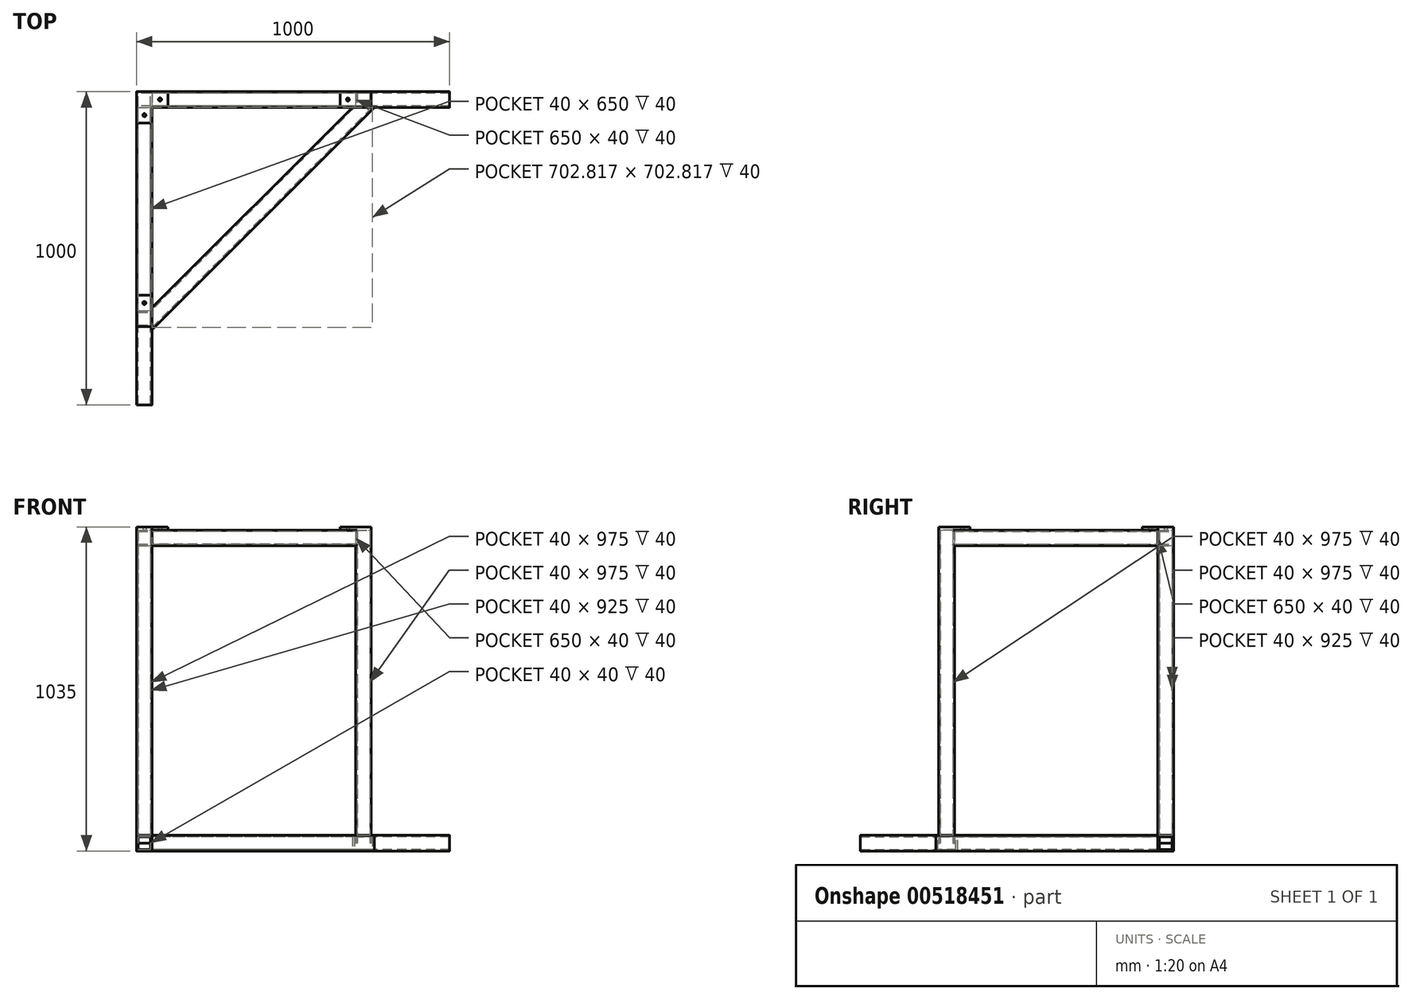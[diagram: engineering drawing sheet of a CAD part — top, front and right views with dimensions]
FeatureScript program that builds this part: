
annotation { "Feature Type Name" : "Feature", "Feature Type Description" : "" }
export const myFeature = defineFeature(function(context is Context, id is Id, definition is map)
    precondition{}
    {
        {
            var Q0;
            Q0=qCreatedBy(makeId("Right.planeOp"),FACE);
            var sketch = newSketch(context, id + "F0", { "sketchPlane" : qUnion([Q0])});
            skLineSegment(sketch, "E0.bottom", {"start": v(20, -25) * mm, "end": v(-20, -25) * mm});
            skLineSegment(sketch, "E0.top", {"start": v(20, 25) * mm, "end": v(-20, 25) * mm});
            skLineSegment(sketch, "E0.left", {"start": v(25, -20) * mm, "end": v(25, 20) * mm});
            skLineSegment(sketch, "E0.right", {"start": v(-25, -20) * mm, "end": v(-25, 20) * mm});
            skPoint(sketch, "E0.middle", {"position": v(0, 0) * mm});
            skLineSegment(sketch, "E1.bottom", {"start": v(20, -20) * mm, "end": v(-20, -20) * mm});
            skLineSegment(sketch, "E1.top", {"start": v(20, 20) * mm, "end": v(-20, 20) * mm});
            skLineSegment(sketch, "E1.left", {"start": v(20, -20) * mm, "end": v(20, 20) * mm});
            skLineSegment(sketch, "E1.right", {"start": v(-20, -20) * mm, "end": v(-20, 20) * mm});
            skPoint(sketch, "E2.visualSharp", {"position": v(-25, 25) * mm});
            skArc(sketch, "E2.filletArc", {"start": v(-20, 25) * mm, "mid": v(-23.54, 23.54) * mm, "end": v(-25, 20) * mm});
            skPoint(sketch, "E3.visualSharp", {"position": v(25, 25) * mm});
            skArc(sketch, "E3.filletArc", {"start": v(25, 20) * mm, "mid": v(23.54, 23.54) * mm, "end": v(20, 25) * mm});
            skPoint(sketch, "E4.visualSharp", {"position": v(25, -25) * mm});
            skArc(sketch, "E4.filletArc", {"start": v(20, -25) * mm, "mid": v(23.54, -23.54) * mm, "end": v(25, -20) * mm});
            skPoint(sketch, "E5.visualSharp", {"position": v(-25, -25) * mm});
            skArc(sketch, "E5.filletArc", {"start": v(-25, -20) * mm, "mid": v(-23.54, -23.54) * mm, "end": v(-20, -25) * mm});
            skSolve(sketch);
        }
        {
            var Q0;
            Q0 = qSketchRegion(id + "F0", true);
            extrude(context, id + "F1", {"entities" : qUnion([Q0]), "depth" : 1000 * mm, "offsetDistance" : 25 * mm});
        }
        {
            var Q0;
            Q0=makeQuery(id+"F1.opExtrude","SWEPT_FACE",FACE,{"disambiguationData":[OSD([sQuery(id+"F0.wireOp",EDGE,"E0.left")])]});
            var sketch = newSketch(context, id + "F2", { "sketchPlane" : qUnion([Q0])});
            skLineSegment(sketch, "E6.bottom", {"start": v(-45, 25) * mm, "end": v(-5, 25) * mm});
            skLineSegment(sketch, "E6.top", {"start": v(-45, -25) * mm, "end": v(-5, -25) * mm});
            skLineSegment(sketch, "E6.left", {"start": v(-50, 20) * mm, "end": v(-50, -20) * mm});
            skLineSegment(sketch, "E6.right", {"start": v(0, 20) * mm, "end": v(0, -20) * mm});
            skLineSegment(sketch, "E7.bottom", {"start": v(-5, -20) * mm, "end": v(-45, -20) * mm});
            skLineSegment(sketch, "E7.top", {"start": v(-5, 20) * mm, "end": v(-45, 20) * mm});
            skLineSegment(sketch, "E7.left", {"start": v(-5, -20) * mm, "end": v(-5, 20) * mm});
            skLineSegment(sketch, "E7.right", {"start": v(-45, -20) * mm, "end": v(-45, 20) * mm});
            skPoint(sketch, "E7.middle", {"position": v(-25, 0) * mm});
            skPoint(sketch, "E8.visualSharp", {"position": v(0, 25) * mm});
            skArc(sketch, "E8.filletArc", {"start": v(-45, 25) * mm, "mid": v(-48.54, 23.54) * mm, "end": v(-50, 20) * mm});
            skArc(sketch, "E9.filletArc", {"start": v(0, 20) * mm, "mid": v(-1.46, 23.54) * mm, "end": v(-5, 25) * mm});
            skPoint(sketch, "E10.visualSharp", {"position": v(0, -25) * mm});
            skArc(sketch, "E10.filletArc", {"start": v(-5, -25) * mm, "mid": v(-1.46, -23.54) * mm, "end": v(0, -20) * mm});
            skPoint(sketch, "E11.visualSharp", {"position": v(-50, -25) * mm});
            skArc(sketch, "E11.filletArc", {"start": v(-50, -20) * mm, "mid": v(-48.54, -23.54) * mm, "end": v(-45, -25) * mm});
            skSolve(sketch);
        }
        {
            var Q0;
            Q0 = qSketchRegion(id + "F2", true);
            extrude(context, id + "F3", {"entities" : qUnion([Q0]), "operationType" : NewBodyOperationType.ADD, "oppositeDirection" : true, "depth" : 1000 * mm, "offsetDistance" : 25 * mm});
        }
        {
            var Q0;
            Q0=qCreatedBy(makeId("Front.planeOp"),FACE);
            var sketch = newSketch(context, id + "F4", { "sketchPlane" : qUnion([Q0])});
            skLineSegment(sketch, "E12", {"start": v(0, 0) * mm, "end": v(0, 168.56) * mm, "construction": true});
            skSolve(sketch);
        }
        {
            var Q0;
            Q0=sQuery(id+"F4.wireOp",EDGE,"E12");
            cPlane(context, id + "F5", {"entities" : qUnion([Q0]), "cplaneType" : CPlaneType.LINE_ANGLE, "offset" : 25 * mm, "angle" : 45 * degree, "width" : 150 * mm, "height" : 150 * mm});
        }
        {
            var Q0;
            Q0=qCreatedBy(id+"F5.planeOp",FACE);
            var sketch = newSketch(context, id + "F6", { "sketchPlane" : qUnion([Q0])});
            skLineSegment(sketch, "E13.bottom", {"start": v(-550, -25) * mm, "end": v(-510, -25) * mm});
            skLineSegment(sketch, "E13.top", {"start": v(-550, 25) * mm, "end": v(-510, 25) * mm});
            skLineSegment(sketch, "E13.left", {"start": v(-555, -20) * mm, "end": v(-555, 20) * mm});
            skLineSegment(sketch, "E13.right", {"start": v(-505, -20) * mm, "end": v(-505, 20) * mm});
            skPoint(sketch, "E13.middle", {"position": v(-530, 0) * mm});
            skLineSegment(sketch, "E14.bottom", {"start": v(-550, -20) * mm, "end": v(-510, -20) * mm});
            skLineSegment(sketch, "E14.top", {"start": v(-550, 20) * mm, "end": v(-510, 20) * mm});
            skLineSegment(sketch, "E14.left", {"start": v(-550, -20) * mm, "end": v(-550, 20) * mm});
            skLineSegment(sketch, "E14.right", {"start": v(-510, -20) * mm, "end": v(-510, 20) * mm});
            skPoint(sketch, "E15.visualSharp", {"position": v(-505, 25) * mm});
            skArc(sketch, "E15.filletArc", {"start": v(-505, 20) * mm, "mid": v(-506.46, 23.54) * mm, "end": v(-510, 25) * mm});
            skPoint(sketch, "E16.visualSharp", {"position": v(-555, 25) * mm});
            skArc(sketch, "E16.filletArc", {"start": v(-550, 25) * mm, "mid": v(-553.54, 23.54) * mm, "end": v(-555, 20) * mm});
            skPoint(sketch, "E17.visualSharp", {"position": v(-505, -25) * mm});
            skArc(sketch, "E17.filletArc", {"start": v(-510, -25) * mm, "mid": v(-506.46, -23.54) * mm, "end": v(-505, -20) * mm});
            skPoint(sketch, "E18.visualSharp", {"position": v(-555, -25) * mm});
            skArc(sketch, "E18.filletArc", {"start": v(-555, -20) * mm, "mid": v(-553.54, -23.54) * mm, "end": v(-550, -25) * mm});
            skSolve(sketch);
        }
        {
            var Q0;
            Q0 = qSketchRegion(id + "F6", true);
            extrude(context, id + "F7", {"entities" : qUnion([Q0]), "operationType" : NewBodyOperationType.ADD, "endBound" : BoundingType.UP_TO_NEXT, "depth" : 25 * mm, "offsetDistance" : 25 * mm, "hasSecondDirection" : true, "secondDirectionBound" : SecondDirectionBoundingType.UP_TO_NEXT, "secondDirectionOppositeDirection" : true, "secondDirectionDepth" : 25 * mm});
        }
        {
            var Q0;
            Q0=qCreatedBy(makeId("Top.planeOp"),FACE);
            var sketch = newSketch(context, id + "F8", { "sketchPlane" : qUnion([Q0])});
            skLineSegment(sketch, "E19.bottom", {"start": v(5, 25) * mm, "end": v(45, 25) * mm});
            skLineSegment(sketch, "E19.top", {"start": v(5, -25) * mm, "end": v(45, -25) * mm});
            skLineSegment(sketch, "E19.left", {"start": v(0, 20) * mm, "end": v(0, -20) * mm});
            skLineSegment(sketch, "E19.right", {"start": v(50, 20) * mm, "end": v(50, -20) * mm});
            skLineSegment(sketch, "E20.bottom", {"start": v(5, 20) * mm, "end": v(45, 20) * mm});
            skLineSegment(sketch, "E20.top", {"start": v(5, -20) * mm, "end": v(45, -20) * mm});
            skLineSegment(sketch, "E20.left", {"start": v(5, 20) * mm, "end": v(5, -20) * mm});
            skLineSegment(sketch, "E20.right", {"start": v(45, 20) * mm, "end": v(45, -20) * mm});
            skPoint(sketch, "E21.visualSharp", {"position": v(0, 25) * mm});
            skArc(sketch, "E21.filletArc", {"start": v(5, 25) * mm, "mid": v(1.46, 23.54) * mm, "end": v(0, 20) * mm});
            skPoint(sketch, "E22.visualSharp", {"position": v(50, 25) * mm});
            skArc(sketch, "E22.filletArc", {"start": v(50, 20) * mm, "mid": v(48.54, 23.54) * mm, "end": v(45, 25) * mm});
            skPoint(sketch, "E23.visualSharp", {"position": v(50, -25) * mm});
            skArc(sketch, "E23.filletArc", {"start": v(45, -25) * mm, "mid": v(48.54, -23.54) * mm, "end": v(50, -20) * mm});
            skPoint(sketch, "E24.visualSharp", {"position": v(0, -25) * mm});
            skArc(sketch, "E24.filletArc", {"start": v(0, -20) * mm, "mid": v(1.46, -23.54) * mm, "end": v(5, -25) * mm});
            skLineSegment(sketch, "E25.0.1.0", {"start": v(5, -720) * mm, "end": v(45, -720) * mm});
            skPoint(sketch, "E25.0.1.1", {"position": v(50, -725) * mm});
            skLineSegment(sketch, "E25.0.1.2", {"start": v(5, -680) * mm, "end": v(5, -720) * mm});
            skPoint(sketch, "E25.0.1.3", {"position": v(50, -675) * mm});
            skLineSegment(sketch, "E25.0.1.4", {"start": v(45, -680) * mm, "end": v(45, -720) * mm});
            skLineSegment(sketch, "E25.0.1.5", {"start": v(5, -680) * mm, "end": v(45, -680) * mm});
            skLineSegment(sketch, "E25.0.1.6", {"start": v(50, -680) * mm, "end": v(50, -720) * mm});
            skLineSegment(sketch, "E25.0.1.7", {"start": v(0, -680) * mm, "end": v(0, -720) * mm});
            skLineSegment(sketch, "E25.0.1.8", {"start": v(5, -725) * mm, "end": v(45, -725) * mm});
            skLineSegment(sketch, "E25.0.1.9", {"start": v(5, -675) * mm, "end": v(45, -675) * mm});
            skPoint(sketch, "E25.0.1.10", {"position": v(0, -675) * mm});
            skPoint(sketch, "E25.0.1.11", {"position": v(0, -725) * mm});
            skArc(sketch, "E25.0.1.12", {"start": v(5, -675) * mm, "mid": v(1.46, -676.46) * mm, "end": v(0, -680) * mm});
            skArc(sketch, "E25.0.1.13", {"start": v(50, -680) * mm, "mid": v(48.54, -676.46) * mm, "end": v(45, -675) * mm});
            skArc(sketch, "E25.0.1.14", {"start": v(45, -725) * mm, "mid": v(48.54, -723.54) * mm, "end": v(50, -720) * mm});
            skArc(sketch, "E25.0.1.15", {"start": v(0, -720) * mm, "mid": v(1.46, -723.54) * mm, "end": v(5, -725) * mm});
            skLineSegment(sketch, "E25.1.0.0", {"start": v(705, -20) * mm, "end": v(745, -20) * mm});
            skPoint(sketch, "E25.1.0.1", {"position": v(750, -25) * mm});
            skLineSegment(sketch, "E25.1.0.2", {"start": v(705, 20) * mm, "end": v(705, -20) * mm});
            skPoint(sketch, "E25.1.0.3", {"position": v(750, 25) * mm});
            skLineSegment(sketch, "E25.1.0.4", {"start": v(745, 20) * mm, "end": v(745, -20) * mm});
            skLineSegment(sketch, "E25.1.0.5", {"start": v(705, 20) * mm, "end": v(745, 20) * mm});
            skLineSegment(sketch, "E25.1.0.6", {"start": v(750, 20) * mm, "end": v(750, -20) * mm});
            skLineSegment(sketch, "E25.1.0.7", {"start": v(700, 20) * mm, "end": v(700, -20) * mm});
            skLineSegment(sketch, "E25.1.0.8", {"start": v(705, -25) * mm, "end": v(745, -25) * mm});
            skLineSegment(sketch, "E25.1.0.9", {"start": v(705, 25) * mm, "end": v(745, 25) * mm});
            skPoint(sketch, "E25.1.0.10", {"position": v(700, 25) * mm});
            skPoint(sketch, "E25.1.0.11", {"position": v(700, -25) * mm});
            skArc(sketch, "E25.1.0.12", {"start": v(705, 25) * mm, "mid": v(701.46, 23.54) * mm, "end": v(700, 20) * mm});
            skArc(sketch, "E25.1.0.13", {"start": v(750, 20) * mm, "mid": v(748.54, 23.54) * mm, "end": v(745, 25) * mm});
            skArc(sketch, "E25.1.0.14", {"start": v(745, -25) * mm, "mid": v(748.54, -23.54) * mm, "end": v(750, -20) * mm});
            skArc(sketch, "E25.1.0.15", {"start": v(700, -20) * mm, "mid": v(701.46, -23.54) * mm, "end": v(705, -25) * mm});
            skLineSegment(sketch, "E25.direction1", {"start": v(0, -25) * mm, "end": v(700, -25) * mm, "construction": true});
            skLineSegment(sketch, "E25.direction2", {"start": v(0, -25) * mm, "end": v(0, -725) * mm, "construction": true});
            skSolve(sketch);
        }
        {
            var Q0;
            Q0 = qSketchRegion(id + "F8", true);
            extrude(context, id + "F9", {"entities" : qUnion([Q0]), "operationType" : NewBodyOperationType.ADD, "depth" : 1000 * mm, "offsetDistance" : 25 * mm});
        }
        {
            var Q0;
            Q0=makeQuery(id+"F9.boolean.opBoolean","MERGE",FACE,{"derivedFrom":[makeQuery(id+"F3.boolean.opBoolean","MERGE",FACE,{"derivedFrom":[makeQuery(id+"F1.opExtrude","CAP_FACE",FACE,{"disambiguationData":[OSD([sQuery(id+"F0.wireOp",EDGE,"E0.bottom"),sQuery(id+"F0.wireOp",EDGE,"E0.top"),sQuery(id+"F0.wireOp",EDGE,"E0.left"),sQuery(id+"F0.wireOp",EDGE,"E0.right"),sQuery(id+"F0.wireOp",EDGE,"E1.bottom"),sQuery(id+"F0.wireOp",EDGE,"E1.top"),sQuery(id+"F0.wireOp",EDGE,"E1.left"),sQuery(id+"F0.wireOp",EDGE,"E1.right"),sQuery(id+"F0.wireOp",EDGE,"E2.filletArc"),sQuery(id+"F0.wireOp",EDGE,"E3.filletArc"),sQuery(id+"F0.wireOp",EDGE,"E4.filletArc"),sQuery(id+"F0.wireOp",EDGE,"E5.filletArc")])],"isStart":true}),makeQuery(id+"F3.opExtrude","SWEPT_FACE",FACE,{"disambiguationData":[OSD([sQuery(id+"F2.wireOp",EDGE,"E6.right")])]})]}),makeQuery(id+"F9.opExtrude","SWEPT_FACE",FACE,{"disambiguationData":[OSD([sQuery(id+"F8.wireOp",EDGE,"E19.left")])]}),makeQuery(id+"F9.opExtrude","SWEPT_FACE",FACE,{"disambiguationData":[OSD([sQuery(id+"F8.wireOp",EDGE,"E25.0.1.7")])]})]});
            var sketch = newSketch(context, id + "F10", { "sketchPlane" : qUnion([Q0])});
            skLineSegment(sketch, "E26.bottom", {"start": v(-20, 1000) * mm, "end": v(20, 1000) * mm});
            skLineSegment(sketch, "E26.top", {"start": v(-20, 950) * mm, "end": v(20, 950) * mm});
            skLineSegment(sketch, "E26.left", {"start": v(-25, 995) * mm, "end": v(-25, 955) * mm});
            skLineSegment(sketch, "E26.right", {"start": v(25, 995) * mm, "end": v(25, 955) * mm});
            skLineSegment(sketch, "E27.bottom", {"start": v(-20, 995) * mm, "end": v(20, 995) * mm});
            skLineSegment(sketch, "E27.top", {"start": v(-20, 955) * mm, "end": v(20, 955) * mm});
            skLineSegment(sketch, "E27.left", {"start": v(-20, 995) * mm, "end": v(-20, 955) * mm});
            skLineSegment(sketch, "E27.right", {"start": v(20, 995) * mm, "end": v(20, 955) * mm});
            skPoint(sketch, "E28.visualSharp", {"position": v(-25, 1000) * mm});
            skArc(sketch, "E28.filletArc", {"start": v(-20, 1000) * mm, "mid": v(-23.54, 998.54) * mm, "end": v(-25, 995) * mm});
            skPoint(sketch, "E29.visualSharp", {"position": v(25, 1000) * mm});
            skArc(sketch, "E29.filletArc", {"start": v(25, 995) * mm, "mid": v(23.54, 998.54) * mm, "end": v(20, 1000) * mm});
            skPoint(sketch, "E30.visualSharp", {"position": v(-25, 950) * mm});
            skArc(sketch, "E30.filletArc", {"start": v(-25, 955) * mm, "mid": v(-23.54, 951.46) * mm, "end": v(-20, 950) * mm});
            skPoint(sketch, "E31.visualSharp", {"position": v(25, 950) * mm});
            skArc(sketch, "E31.filletArc", {"start": v(20, 950) * mm, "mid": v(23.54, 951.46) * mm, "end": v(25, 955) * mm});
            skSolve(sketch);
        }
        {
            var Q0;
            Q0 = qSketchRegion(id + "F10", true);
            extrude(context, id + "F11", {"entities" : qUnion([Q0]), "operationType" : NewBodyOperationType.ADD, "oppositeDirection" : true, "depth" : 705 * mm, "offsetDistance" : 25 * mm});
        }
        {
            var Q0;
            Q0=makeQuery(id+"F11.boolean.opBoolean","MERGE",FACE,{"derivedFrom":[makeQuery(id+"F9.boolean.opBoolean","MERGE",FACE,{"derivedFrom":[makeQuery(id+"F3.boolean.opBoolean","MERGE",FACE,{"derivedFrom":[makeQuery(id+"F1.opExtrude","SWEPT_FACE",FACE,{"disambiguationData":[OSD([sQuery(id+"F0.wireOp",EDGE,"E0.left")])]}),makeQuery(id+"F3.opExtrude","CAP_FACE",FACE,{"disambiguationData":[OSD([sQuery(id+"F2.wireOp",EDGE,"E6.bottom"),sQuery(id+"F2.wireOp",EDGE,"E6.top"),sQuery(id+"F2.wireOp",EDGE,"E6.left"),sQuery(id+"F2.wireOp",EDGE,"E6.right"),sQuery(id+"F2.wireOp",EDGE,"E7.bottom"),sQuery(id+"F2.wireOp",EDGE,"E7.top"),sQuery(id+"F2.wireOp",EDGE,"E7.left"),sQuery(id+"F2.wireOp",EDGE,"E7.right"),sQuery(id+"F2.wireOp",EDGE,"E8.filletArc"),sQuery(id+"F2.wireOp",EDGE,"E9.filletArc"),sQuery(id+"F2.wireOp",EDGE,"E10.filletArc"),sQuery(id+"F2.wireOp",EDGE,"E11.filletArc")])],"isStart":true})]}),makeQuery(id+"F9.opExtrude","SWEPT_FACE",FACE,{"disambiguationData":[OSD([sQuery(id+"F8.wireOp",EDGE,"E19.bottom")])]}),makeQuery(id+"F9.opExtrude","SWEPT_FACE",FACE,{"disambiguationData":[OSD([sQuery(id+"F8.wireOp",EDGE,"E25.1.0.9")])]})]}),makeQuery(id+"F11.opExtrude","SWEPT_FACE",FACE,{"disambiguationData":[OSD([sQuery(id+"F10.wireOp",EDGE,"E26.left")])]})]});
            var sketch = newSketch(context, id + "F12", { "sketchPlane" : qUnion([Q0])});
            skLineSegment(sketch, "E32.bottom", {"start": v(-5, 1000) * mm, "end": v(-45, 1000) * mm});
            skLineSegment(sketch, "E32.top", {"start": v(-5, 950) * mm, "end": v(-45, 950) * mm});
            skLineSegment(sketch, "E32.left", {"start": v(0, 995) * mm, "end": v(0, 955) * mm});
            skLineSegment(sketch, "E32.right", {"start": v(-50, 995) * mm, "end": v(-50, 955) * mm});
            skLineSegment(sketch, "E33.bottom", {"start": v(-5, 995) * mm, "end": v(-45, 995) * mm});
            skLineSegment(sketch, "E33.top", {"start": v(-5, 955) * mm, "end": v(-45, 955) * mm});
            skLineSegment(sketch, "E33.left", {"start": v(-5, 995) * mm, "end": v(-5, 955) * mm});
            skLineSegment(sketch, "E33.right", {"start": v(-45, 995) * mm, "end": v(-45, 955) * mm});
            skPoint(sketch, "E34.visualSharp", {"position": v(0, 1000) * mm});
            skArc(sketch, "E34.filletArc", {"start": v(0, 995) * mm, "mid": v(-1.46, 998.54) * mm, "end": v(-5, 1000) * mm});
            skPoint(sketch, "E35.visualSharp", {"position": v(-50, 1000) * mm});
            skArc(sketch, "E35.filletArc", {"start": v(-45, 1000) * mm, "mid": v(-48.54, 998.54) * mm, "end": v(-50, 995) * mm});
            skPoint(sketch, "E36.visualSharp", {"position": v(-50, 950) * mm});
            skArc(sketch, "E36.filletArc", {"start": v(-50, 955) * mm, "mid": v(-48.54, 951.46) * mm, "end": v(-45, 950) * mm});
            skPoint(sketch, "E37.visualSharp", {"position": v(0, 950) * mm});
            skArc(sketch, "E37.filletArc", {"start": v(-5, 950) * mm, "mid": v(-1.46, 951.46) * mm, "end": v(0, 955) * mm});
            skSolve(sketch);
        }
        {
            var Q0;
            Q0 = qSketchRegion(id + "F12", true);
            extrude(context, id + "F13", {"entities" : qUnion([Q0]), "operationType" : NewBodyOperationType.ADD, "oppositeDirection" : true, "depth" : 705 * mm, "offsetDistance" : 25 * mm});
        }
        {
            var Q0;
            Q0=makeQuery(id+"F13.boolean.opBoolean","MERGE",FACE,{"derivedFrom":[makeQuery(id+"F9.opExtrude","CAP_FACE",FACE,{"disambiguationData":[OSD([sQuery(id+"F8.wireOp",EDGE,"E25.0.1.0"),sQuery(id+"F8.wireOp",EDGE,"E25.0.1.2"),sQuery(id+"F8.wireOp",EDGE,"E25.0.1.4"),sQuery(id+"F8.wireOp",EDGE,"E25.0.1.5"),sQuery(id+"F8.wireOp",EDGE,"E25.0.1.6"),sQuery(id+"F8.wireOp",EDGE,"E25.0.1.7"),sQuery(id+"F8.wireOp",EDGE,"E25.0.1.8"),sQuery(id+"F8.wireOp",EDGE,"E25.0.1.9"),sQuery(id+"F8.wireOp",EDGE,"E25.0.1.12"),sQuery(id+"F8.wireOp",EDGE,"E25.0.1.13"),sQuery(id+"F8.wireOp",EDGE,"E25.0.1.14"),sQuery(id+"F8.wireOp",EDGE,"E25.0.1.15")])],"isStart":false}),makeQuery(id+"F11.boolean.opBoolean","MERGE",FACE,{"derivedFrom":[makeQuery(id+"F9.opExtrude","CAP_FACE",FACE,{"disambiguationData":[OSD([sQuery(id+"F8.wireOp",EDGE,"E19.bottom"),sQuery(id+"F8.wireOp",EDGE,"E19.top"),sQuery(id+"F8.wireOp",EDGE,"E19.left"),sQuery(id+"F8.wireOp",EDGE,"E19.right"),sQuery(id+"F8.wireOp",EDGE,"E20.bottom"),sQuery(id+"F8.wireOp",EDGE,"E20.top"),sQuery(id+"F8.wireOp",EDGE,"E20.left"),sQuery(id+"F8.wireOp",EDGE,"E20.right"),sQuery(id+"F8.wireOp",EDGE,"E21.filletArc"),sQuery(id+"F8.wireOp",EDGE,"E22.filletArc"),sQuery(id+"F8.wireOp",EDGE,"E23.filletArc"),sQuery(id+"F8.wireOp",EDGE,"E24.filletArc")])],"isStart":false}),makeQuery(id+"F9.opExtrude","CAP_FACE",FACE,{"disambiguationData":[OSD([sQuery(id+"F8.wireOp",EDGE,"E25.1.0.0"),sQuery(id+"F8.wireOp",EDGE,"E25.1.0.2"),sQuery(id+"F8.wireOp",EDGE,"E25.1.0.4"),sQuery(id+"F8.wireOp",EDGE,"E25.1.0.5"),sQuery(id+"F8.wireOp",EDGE,"E25.1.0.6"),sQuery(id+"F8.wireOp",EDGE,"E25.1.0.7"),sQuery(id+"F8.wireOp",EDGE,"E25.1.0.8"),sQuery(id+"F8.wireOp",EDGE,"E25.1.0.9"),sQuery(id+"F8.wireOp",EDGE,"E25.1.0.12"),sQuery(id+"F8.wireOp",EDGE,"E25.1.0.13"),sQuery(id+"F8.wireOp",EDGE,"E25.1.0.14"),sQuery(id+"F8.wireOp",EDGE,"E25.1.0.15")])],"isStart":false}),makeQuery(id+"F11.opExtrude","SWEPT_FACE",FACE,{"disambiguationData":[OSD([sQuery(id+"F10.wireOp",EDGE,"E26.bottom")])]})]}),makeQuery(id+"F13.opExtrude","SWEPT_FACE",FACE,{"disambiguationData":[OSD([sQuery(id+"F12.wireOp",EDGE,"E32.bottom")])]})]});
            var sketch = newSketch(context, id + "F14", { "sketchPlane" : qUnion([Q0])});
            skLineSegment(sketch, "E38.bottom", {"start": v(0, 25) * mm, "end": v(100, 24.76) * mm});
            skLineSegment(sketch, "E38.left", {"start": v(0, 25) * mm, "end": v(0, -75) * mm});
            skLineSegment(sketch, "E38.right", {"start": v(100, 24.76) * mm, "end": v(100, -25.24) * mm});
            skLineSegment(sketch, "E39", {"start": v(0, -75) * mm, "end": v(50, -75) * mm});
            skLineSegment(sketch, "E40", {"start": v(50, -75) * mm, "end": v(50, -25) * mm});
            skLineSegment(sketch, "E41", {"start": v(50, -25) * mm, "end": v(100, -25.24) * mm});
            skLineSegment(sketch, "E42.bottom", {"start": v(650, -25) * mm, "end": v(750, -25) * mm});
            skLineSegment(sketch, "E42.top", {"start": v(650, 25) * mm, "end": v(750, 25) * mm});
            skLineSegment(sketch, "E42.left", {"start": v(650, -25) * mm, "end": v(650, 25) * mm});
            skLineSegment(sketch, "E42.right", {"start": v(750, -25) * mm, "end": v(750, 25) * mm});
            skLineSegment(sketch, "E43.bottom", {"start": v(0, -725) * mm, "end": v(50, -725) * mm});
            skLineSegment(sketch, "E43.top", {"start": v(0, -625) * mm, "end": v(50, -625) * mm});
            skLineSegment(sketch, "E43.left", {"start": v(0, -725) * mm, "end": v(0, -625) * mm});
            skLineSegment(sketch, "E43.right", {"start": v(50, -725) * mm, "end": v(50, -625) * mm});
            skCircle(sketch, "E44", {"center": v(75, 0) * mm, "radius": 5 * mm});
            skCircle(sketch, "E45", {"center": v(25, -50.06) * mm, "radius": 5 * mm});
            skCircle(sketch, "E46", {"center": v(675, 0) * mm, "radius": 5 * mm});
            skCircle(sketch, "E47", {"center": v(25, -650) * mm, "radius": 5 * mm});
            skPoint(sketch, "E47.centerSnap0", {"position": v(25, -680) * mm});
            skSolve(sketch);
        }
        {
            var Q0;
            Q0 = qSketchRegion(id + "F14", true);
            extrude(context, id + "F15", {"entities" : qUnion([Q0]), "operationType" : NewBodyOperationType.ADD, "depth" : 10 * mm, "offsetDistance" : 25 * mm});
        }
    });
